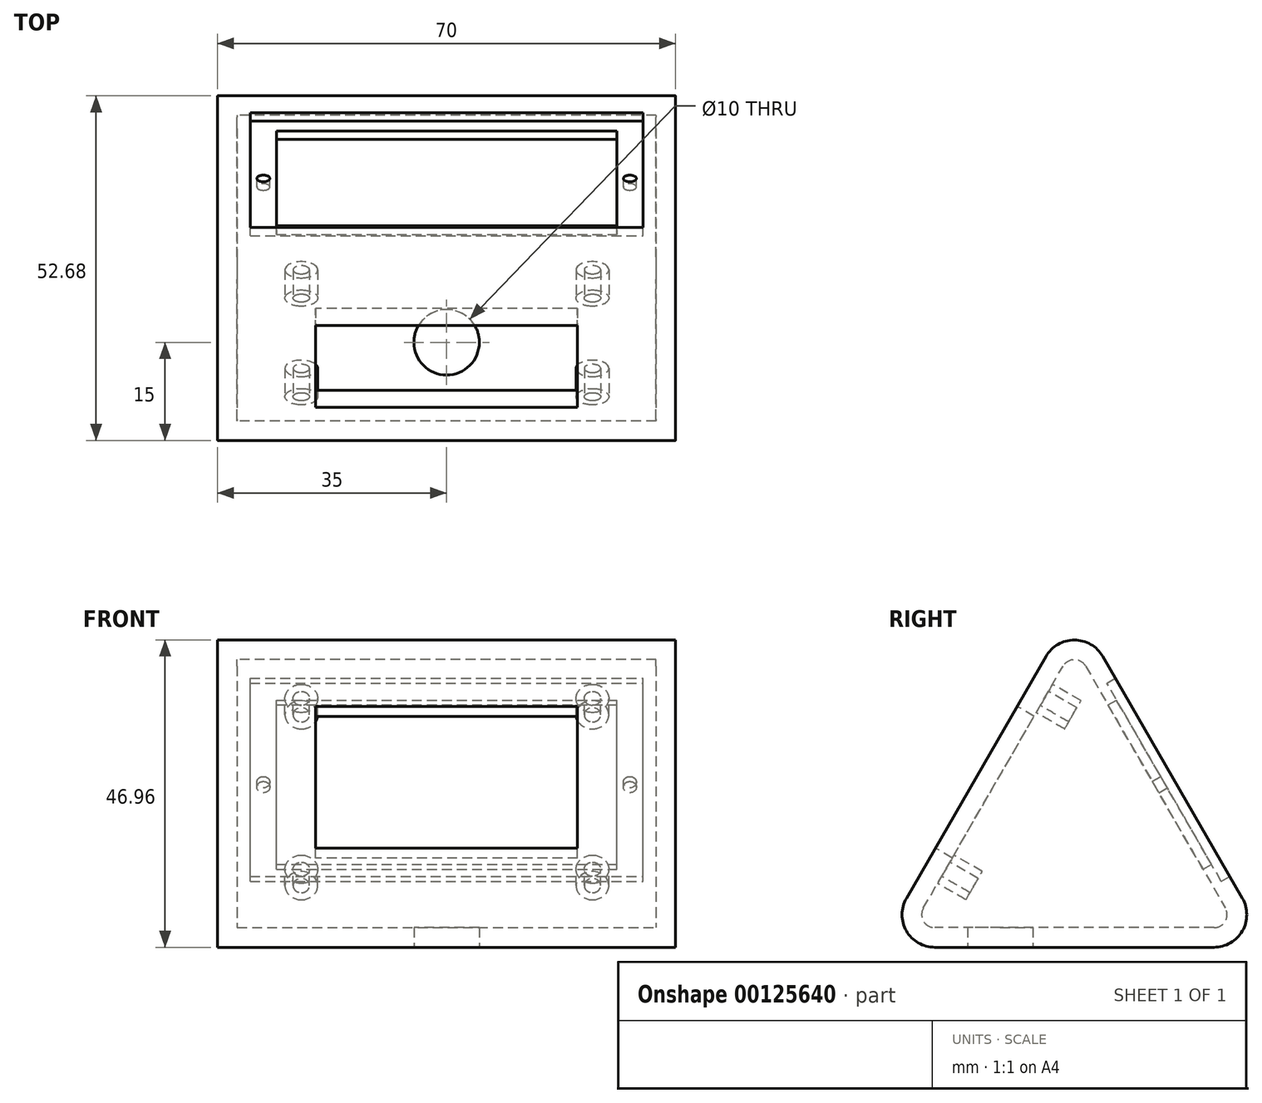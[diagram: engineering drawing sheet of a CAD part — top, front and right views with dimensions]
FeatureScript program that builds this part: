
annotation { "Feature Type Name" : "Feature", "Feature Type Description" : "" }
export const myFeature = defineFeature(function(context is Context, id is Id, definition is map)
    precondition{}
    {
        {
            var Q0;
            Q0=qCreatedBy(makeId("Right.planeOp"),FACE);
            var sketch = newSketch(context, id + "F0", { "sketchPlane" : qUnion([Q0])});
            skLineSegment(sketch, "E0", {"start": v(0, 0) * mm, "end": v(-30, 51.96) * mm});
            skLineSegment(sketch, "E1", {"start": v(-30, 51.96) * mm, "end": v(-60, 0) * mm});
            skLineSegment(sketch, "E2", {"start": v(-60, 0) * mm, "end": v(0, 0) * mm});
            skLineSegment(sketch, "E3", {"start": v(-54.8, 3) * mm, "end": v(-30, 45.96) * mm});
            skLineSegment(sketch, "E4", {"start": v(-30, 45.96) * mm, "end": v(-5.2, 3) * mm});
            skLineSegment(sketch, "E5", {"start": v(-5.2, 3) * mm, "end": v(-54.8, 3) * mm});
            skSolve(sketch);
        }
        {
            var Q0;
            Q0=makeQuery(id+"F0.imprint","IMPRINT",FACE,{"disambiguationData":[TD([[makeQuery(id+"F0.imprint","IMPRINT",EDGE,{"derivedFrom":sQuery(id+"F0.wireOp",EDGE,"E0")}),1.0]])]});
            var Q1;
            Q1=makeQuery(id+"F0.imprint","IMPRINT",FACE,{"disambiguationData":[TD([[makeQuery(id+"F0.imprint","IMPRINT",EDGE,{"derivedFrom":sQuery(id+"F0.wireOp",EDGE,"E3")}),-1.0]])]});
            extrude(context, id + "F1", {"entities" : qUnion([Q0, Q1]), "endBound" : BoundingType.SYMMETRIC, "depth" : 70 * mm, "offsetDistance" : 25 * mm});
        }
        {
            var Q0;
            Q0=makeQuery(id+"F0.imprint","IMPRINT",FACE,{"disambiguationData":[TD([[makeQuery(id+"F0.imprint","IMPRINT",EDGE,{"derivedFrom":sQuery(id+"F0.wireOp",EDGE,"E3")}),-1.0]])]});
            extrude(context, id + "F2", {"entities" : qUnion([Q0]), "operationType" : NewBodyOperationType.REMOVE, "endBound" : BoundingType.SYMMETRIC, "oppositeDirection" : true, "depth" : 64 * mm, "offsetDistance" : 25 * mm});
        }
        {
            var Q0;
            Q0=makeQuery(id+"F1.opExtrude","SWEPT_EDGE",EDGE,{"disambiguationData":[OSD([sQuery(id+"F0.wireOp",EDGE,"E0"),sQuery(id+"F0.wireOp",EDGE,"E1")])]});
            var Q1;
            Q1=makeQuery(id+"F1.opExtrude","SWEPT_EDGE",EDGE,{"disambiguationData":[OSD([sQuery(id+"F0.wireOp",EDGE,"E1"),sQuery(id+"F0.wireOp",EDGE,"E2")])]});
            var Q2;
            Q2=makeQuery(id+"F1.opExtrude","SWEPT_EDGE",EDGE,{"disambiguationData":[OSD([sQuery(id+"F0.wireOp",EDGE,"E0"),sQuery(id+"F0.wireOp",EDGE,"E2")])]});
            fillet(context, id + "F3", {"entities" : qUnion([Q0, Q1, Q2]), "radius" : 5 * mm, "tangentPropagation" : true, "allowEdgeOverflow" : false});
        }
        {
            var Q0;
            Q0=makeQuery(id+"F2.boolean.opBoolean","COPY",EDGE,{"derivedFrom":makeQuery(id+"F2.opExtrude","SWEPT_EDGE",EDGE,{"disambiguationData":[OSD([sQuery(id+"F0.wireOp",EDGE,"E3"),sQuery(id+"F0.wireOp",EDGE,"E4")])]})});
            var Q1;
            Q1=makeQuery(id+"F2.boolean.opBoolean","COPY",EDGE,{"derivedFrom":makeQuery(id+"F2.opExtrude","SWEPT_EDGE",EDGE,{"disambiguationData":[OSD([sQuery(id+"F0.wireOp",EDGE,"E4"),sQuery(id+"F0.wireOp",EDGE,"E5")])]})});
            var Q2;
            Q2=makeQuery(id+"F2.boolean.opBoolean","COPY",EDGE,{"derivedFrom":makeQuery(id+"F2.opExtrude","SWEPT_EDGE",EDGE,{"disambiguationData":[OSD([sQuery(id+"F0.wireOp",EDGE,"E3"),sQuery(id+"F0.wireOp",EDGE,"E5")])]})});
            fillet(context, id + "F4", {"entities" : qUnion([Q0, Q1, Q2]), "radius" : 2 * mm, "tangentPropagation" : true, "allowEdgeOverflow" : false});
        }
        {
            var Q0;
            Q0=makeQuery(id+"F1.opExtrude","SWEPT_FACE",FACE,{"disambiguationData":[OSD([sQuery(id+"F0.wireOp",EDGE,"E1")])]});
            var sketch = newSketch(context, id + "F5", { "sketchPlane" : qUnion([Q0])});
            skLineSegment(sketch, "E6.bottom", {"start": v(20, -12.5) * mm, "end": v(-20, -12.5) * mm});
            skLineSegment(sketch, "E6.top", {"start": v(20, 12.5) * mm, "end": v(-20, 12.5) * mm});
            skLineSegment(sketch, "E6.left", {"start": v(20, -12.5) * mm, "end": v(20, 12.5) * mm});
            skLineSegment(sketch, "E6.right", {"start": v(-20, -12.5) * mm, "end": v(-20, 12.5) * mm});
            skCircle(sketch, "E7", {"center": v(-22.2, 15.65) * mm, "radius": 2.5 * mm});
            skCircle(sketch, "E8", {"center": v(-22.2, -14.5) * mm, "radius": 2.5 * mm});
            skCircle(sketch, "E9", {"center": v(22.29, -14.5) * mm, "radius": 2.5 * mm});
            skCircle(sketch, "E10", {"center": v(22.29, 15.65) * mm, "radius": 2.5 * mm});
            skCircle(sketch, "E11", {"center": v(-22.2, 15.65) * mm, "radius": 1.25 * mm});
            skCircle(sketch, "E12", {"center": v(22.29, 15.65) * mm, "radius": 1.25 * mm});
            skCircle(sketch, "E13", {"center": v(22.29, -14.5) * mm, "radius": 1.25 * mm});
            skCircle(sketch, "E14", {"center": v(-22.2, -14.5) * mm, "radius": 1.25 * mm});
            skSolve(sketch);
        }
        {
            var Q0;
            Q0=makeQuery(id+"F5.imprint","IMPRINT",FACE,{"disambiguationData":[TD([[makeQuery(id+"F5.imprint","IMPRINT",EDGE,{"derivedFrom":sQuery(id+"F5.wireOp",EDGE,"E6.bottom")}),-1.0]])]});
            extrude(context, id + "F6", {"entities" : qUnion([Q0]), "operationType" : NewBodyOperationType.REMOVE, "oppositeDirection" : true, "depth" : 3 * mm, "offsetDistance" : 25 * mm});
        }
        {
            var Q0;
            Q0=makeQuery(id+"F5.imprint","IMPRINT",FACE,{"disambiguationData":[TD([[makeQuery(id+"F5.imprint","IMPRINT",EDGE,{"derivedFrom":sQuery(id+"F5.wireOp",EDGE,"E7")}),1.0]])]});
            var Q1;
            Q1=makeQuery(id+"F5.imprint","IMPRINT",FACE,{"disambiguationData":[TD([[makeQuery(id+"F5.imprint","IMPRINT",EDGE,{"derivedFrom":sQuery(id+"F5.wireOp",EDGE,"E10")}),1.0]])]});
            var Q2;
            Q2=makeQuery(id+"F5.imprint","IMPRINT",FACE,{"disambiguationData":[TD([[makeQuery(id+"F5.imprint","IMPRINT",EDGE,{"derivedFrom":sQuery(id+"F5.wireOp",EDGE,"E9")}),1.0]])]});
            var Q3;
            Q3=makeQuery(id+"F5.imprint","IMPRINT",FACE,{"disambiguationData":[TD([[makeQuery(id+"F5.imprint","IMPRINT",EDGE,{"derivedFrom":sQuery(id+"F5.wireOp",EDGE,"E8")}),1.0]])]});
            extrude(context, id + "F7", {"entities" : qUnion([Q0, Q1, Q2, Q3]), "operationType" : NewBodyOperationType.ADD, "oppositeDirection" : true, "depth" : 8 * mm, "offsetDistance" : 25 * mm});
        }
        {
            var Q0;
            Q0=makeQuery(id+"F1.opExtrude","SWEPT_FACE",FACE,{"disambiguationData":[OSD([sQuery(id+"F0.wireOp",EDGE,"E0")])]});
            var sketch = newSketch(context, id + "F8", { "sketchPlane" : qUnion([Q0])});
            skLineSegment(sketch, "E15.bottom", {"start": v(30, 12.5) * mm, "end": v(-30, 12.5) * mm});
            skLineSegment(sketch, "E15.top", {"start": v(30, 47.5) * mm, "end": v(-30, 47.5) * mm});
            skLineSegment(sketch, "E15.left", {"start": v(30, 12.5) * mm, "end": v(30, 47.5) * mm});
            skLineSegment(sketch, "E15.right", {"start": v(-30, 12.5) * mm, "end": v(-30, 47.5) * mm});
            skLineSegment(sketch, "E16.bottom", {"start": v(26, 15.5) * mm, "end": v(-26, 15.5) * mm});
            skLineSegment(sketch, "E16.top", {"start": v(26, 44.5) * mm, "end": v(-26, 44.5) * mm});
            skLineSegment(sketch, "E16.left", {"start": v(26, 15.5) * mm, "end": v(26, 44.5) * mm});
            skLineSegment(sketch, "E16.right", {"start": v(-26, 15.5) * mm, "end": v(-26, 44.5) * mm});
            skPoint(sketch, "E16.middle", {"position": v(0, 30) * mm});
            skPoint(sketch, "E17.positionSnap0", {"position": v(26, 30) * mm});
            skPoint(sketch, "E18", {"position": v(28, 30) * mm});
            skPoint(sketch, "E19", {"position": v(-28, 30) * mm});
            skPoint(sketch, "E19.positionSnap0", {"position": v(-26, 30) * mm});
            skSolve(sketch);
        }
        {
            var Q0;
            Q0=makeQuery(id+"F8.imprint","IMPRINT",FACE,{"disambiguationData":[TD([[makeQuery(id+"F8.imprint","IMPRINT",EDGE,{"derivedFrom":sQuery(id+"F8.wireOp",EDGE,"E16.bottom")}),-1.0]])]});
            extrude(context, id + "F9", {"entities" : qUnion([Q0]), "operationType" : NewBodyOperationType.REMOVE, "oppositeDirection" : true, "depth" : 3 * mm, "offsetDistance" : 25 * mm});
        }
        {
            var Q0;
            Q0=makeQuery(id+"F8.imprint","IMPRINT",FACE,{"disambiguationData":[TD([[makeQuery(id+"F8.imprint","IMPRINT",EDGE,{"derivedFrom":sQuery(id+"F8.wireOp",EDGE,"E15.bottom")}),-1.0]])]});
            extrude(context, id + "F10", {"entities" : qUnion([Q0]), "operationType" : NewBodyOperationType.REMOVE, "oppositeDirection" : true, "depth" : 1.5 * mm, "offsetDistance" : 25 * mm});
        }
        {
            var Q0;
            Q0=makeQuery(id+"F1.opExtrude","SWEPT_FACE",FACE,{"disambiguationData":[OSD([sQuery(id+"F0.wireOp",EDGE,"E2")])]});
            var sketch = newSketch(context, id + "F11", { "sketchPlane" : qUnion([Q0])});
            skCircle(sketch, "E20", {"center": v(0, 41.34) * mm, "radius": 5 * mm});
            skSolve(sketch);
        }
        {
            var Q0;
            Q0=makeQuery(id+"F11.imprint","IMPRINT",FACE,{"disambiguationData":[TD([[makeQuery(id+"F11.imprint","IMPRINT",EDGE,{"derivedFrom":sQuery(id+"F11.wireOp",EDGE,"E20")}),1.0]])]});
            extrude(context, id + "F12", {"entities" : qUnion([Q0]), "operationType" : NewBodyOperationType.REMOVE, "endBound" : BoundingType.UP_TO_NEXT, "oppositeDirection" : true, "depth" : 25 * mm, "offsetDistance" : 25 * mm});
        }
        {
            var Q0;
            Q0=sQuery(id+"F8.wireOp",VERTEX,"E19");
            var Q1;
            Q1=sQuery(id+"F8.wireOp",VERTEX,"E18");
            var Q2;
            Q2=makeQuery(id+"F1.opExtrude","SWEPT_BODY",BODY,{"disambiguationData":[OSD([sQuery(id+"F0.wireOp",EDGE,"E0"),sQuery(id+"F0.wireOp",EDGE,"E1"),sQuery(id+"F0.wireOp",EDGE,"E2")])]});
            hole(context, id + "F13", {"style" : HoleStyle.SIMPLE, "endStyle" : HoleEndStyle.BLIND, "holeDiameter" : 2 * mm, "holeDepth" : 3 * mm, "tappedDepth" : 12 * mm, "tapClearance" : 3, "startFromSketch" : true, "locations" : qUnion([Q0, Q1]), "scope" : qUnion([Q2])});
        }
    });
